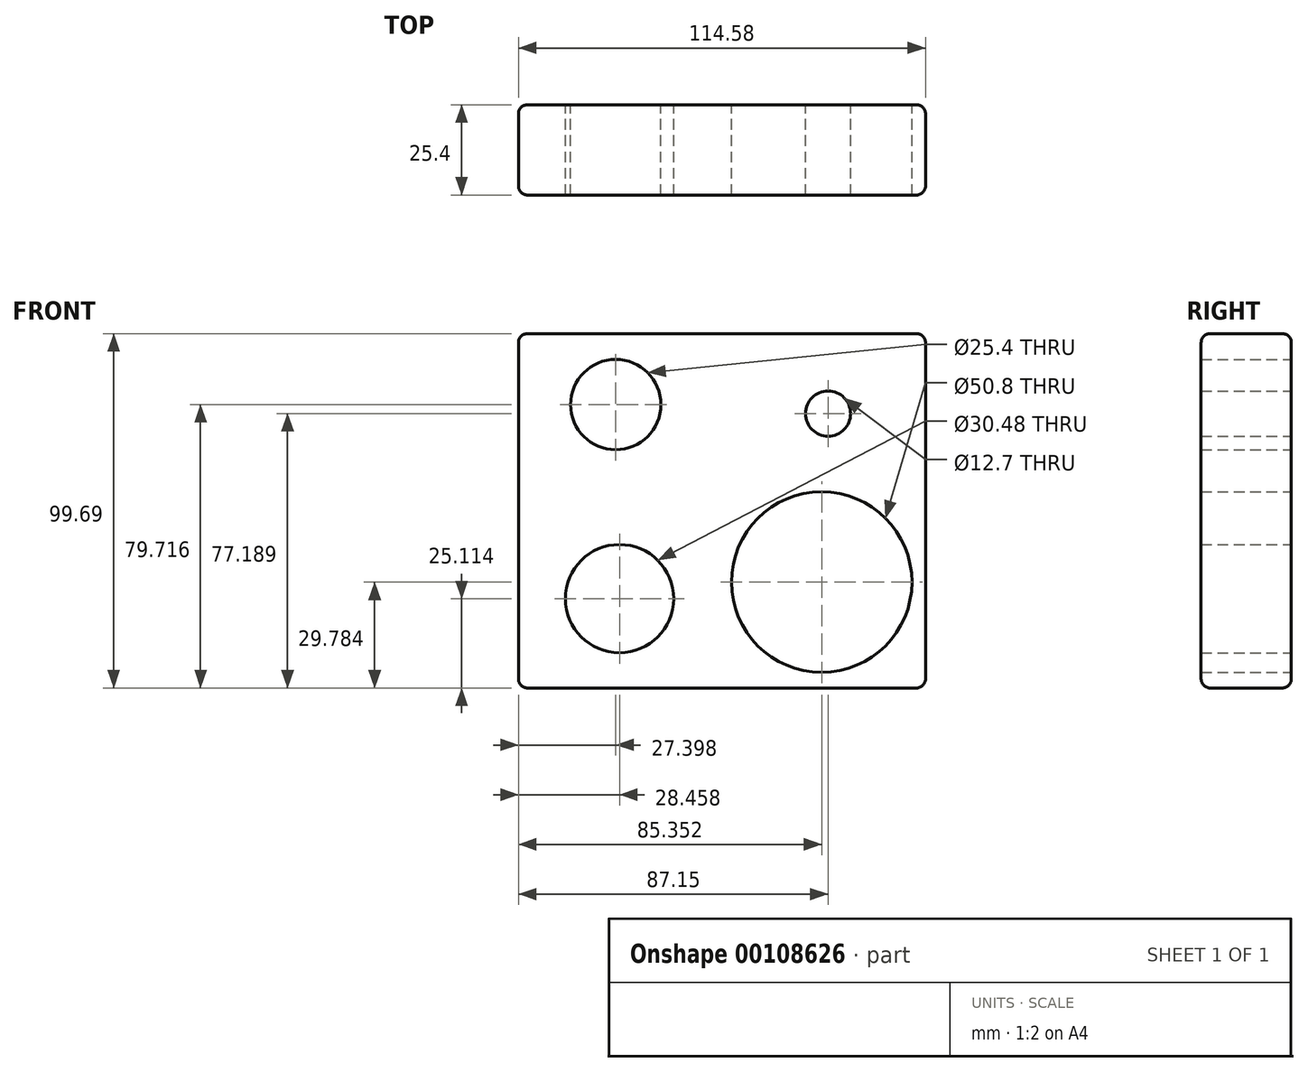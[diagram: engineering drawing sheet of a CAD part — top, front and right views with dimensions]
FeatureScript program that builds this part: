
annotation { "Feature Type Name" : "Feature", "Feature Type Description" : "" }
export const myFeature = defineFeature(function(context is Context, id is Id, definition is map)
    precondition{}
    {
        {
            var Q0;
            Q0=qCreatedBy(makeId("Front.planeOp"),FACE);
            var sketch = newSketch(context, id + "F0", { "sketchPlane" : qUnion([Q0])});
            skLineSegment(sketch, "E0.bottom", {"start": v(-57.29, 48.81) * mm, "end": v(57.29, 48.81) * mm});
            skLineSegment(sketch, "E0.top", {"start": v(-57.29, -50.88) * mm, "end": v(57.29, -50.88) * mm});
            skLineSegment(sketch, "E0.left", {"start": v(-57.29, 48.81) * mm, "end": v(-57.29, -50.88) * mm});
            skLineSegment(sketch, "E0.right", {"start": v(57.29, 48.81) * mm, "end": v(57.29, -50.88) * mm});
            skSolve(sketch);
        }
        {
            var Q0;
            Q0=makeQuery(id+"F0.imprint","IMPRINT",FACE,{"disambiguationData":[TD([[makeQuery(id+"F0.imprint","IMPRINT",EDGE,{"derivedFrom":sQuery(id+"F0.wireOp",EDGE,"E0.bottom")}),-1.0]])]});
            extrude(context, id + "F1", {"entities" : qUnion([Q0]), "depth" : 25.4 * mm});
        }
        {
            var Q0;
            Q0=qCreatedBy(makeId("Front.planeOp"),FACE);
            var sketch = newSketch(context, id + "F2", { "sketchPlane" : qUnion([Q0])});
            skCircle(sketch, "E1", {"center": v(-29.9, 28.84) * mm, "radius": 12.7 * mm});
            skCircle(sketch, "E2", {"center": v(29.86, 26.3) * mm, "radius": 6.35 * mm});
            skCircle(sketch, "E3", {"center": v(-28.83, -25.77) * mm, "radius": 15.24 * mm});
            skCircle(sketch, "E4", {"center": v(28.06, -21.1) * mm, "radius": 25.4 * mm});
            skSolve(sketch);
        }
        {
            var Q0;
            Q0 = qSketchRegion(id + "F2", true);
            extrude(context, id + "F3", {"entities" : qUnion([Q0]), "operationType" : NewBodyOperationType.REMOVE, "depth" : 25.4 * mm});
        }
        {
            var Q0;
            Q0=makeQuery(id+"F1.opExtrude","CAP_EDGE",EDGE,{"disambiguationData":[OSD([sQuery(id+"F0.wireOp",EDGE,"E0.bottom")])],"isStart":false});
            var Q1;
            Q1=makeQuery(id+"F1.opExtrude","SWEPT_EDGE",EDGE,{"disambiguationData":[OSD([sQuery(id+"F0.wireOp",EDGE,"E0.bottom"),sQuery(id+"F0.wireOp",EDGE,"E0.left")])]});
            var Q2;
            Q2=makeQuery(id+"F1.opExtrude","CAP_EDGE",EDGE,{"disambiguationData":[OSD([sQuery(id+"F0.wireOp",EDGE,"E0.bottom")])],"isStart":true});
            var Q3;
            Q3=makeQuery(id+"F1.opExtrude","SWEPT_EDGE",EDGE,{"disambiguationData":[OSD([sQuery(id+"F0.wireOp",EDGE,"E0.bottom"),sQuery(id+"F0.wireOp",EDGE,"E0.right")])]});
            var Q4;
            Q4=makeQuery(id+"F1.opExtrude","CAP_EDGE",EDGE,{"disambiguationData":[OSD([sQuery(id+"F0.wireOp",EDGE,"E0.right")])],"isStart":false});
            var Q5;
            Q5=makeQuery(id+"F1.opExtrude","CAP_EDGE",EDGE,{"disambiguationData":[OSD([sQuery(id+"F0.wireOp",EDGE,"E0.right")])],"isStart":true});
            var Q6;
            Q6=makeQuery(id+"F1.opExtrude","CAP_EDGE",EDGE,{"disambiguationData":[OSD([sQuery(id+"F0.wireOp",EDGE,"E0.left")])],"isStart":false});
            var Q7;
            Q7=makeQuery(id+"F1.opExtrude","CAP_EDGE",EDGE,{"disambiguationData":[OSD([sQuery(id+"F0.wireOp",EDGE,"E0.top")])],"isStart":false});
            var Q8;
            Q8=makeQuery(id+"F1.opExtrude","SWEPT_EDGE",EDGE,{"disambiguationData":[OSD([sQuery(id+"F0.wireOp",EDGE,"E0.top"),sQuery(id+"F0.wireOp",EDGE,"E0.right")])]});
            var Q9;
            Q9=makeQuery(id+"F1.opExtrude","CAP_EDGE",EDGE,{"disambiguationData":[OSD([sQuery(id+"F0.wireOp",EDGE,"E0.top")])],"isStart":true});
            var Q10;
            Q10=makeQuery(id+"F1.opExtrude","SWEPT_EDGE",EDGE,{"disambiguationData":[OSD([sQuery(id+"F0.wireOp",EDGE,"E0.top"),sQuery(id+"F0.wireOp",EDGE,"E0.left")])]});
            var Q11;
            Q11=makeQuery(id+"F1.opExtrude","CAP_EDGE",EDGE,{"disambiguationData":[OSD([sQuery(id+"F0.wireOp",EDGE,"E0.left")])],"isStart":true});
            fillet(context, id + "F4", {"entities" : qUnion([Q0, Q1, Q2, Q3, Q4, Q5, Q6, Q7, Q8, Q9, Q10, Q11]), "radius" : 2.54 * mm, "tangentPropagation" : true, "allowEdgeOverflow" : false});
        }
    });
